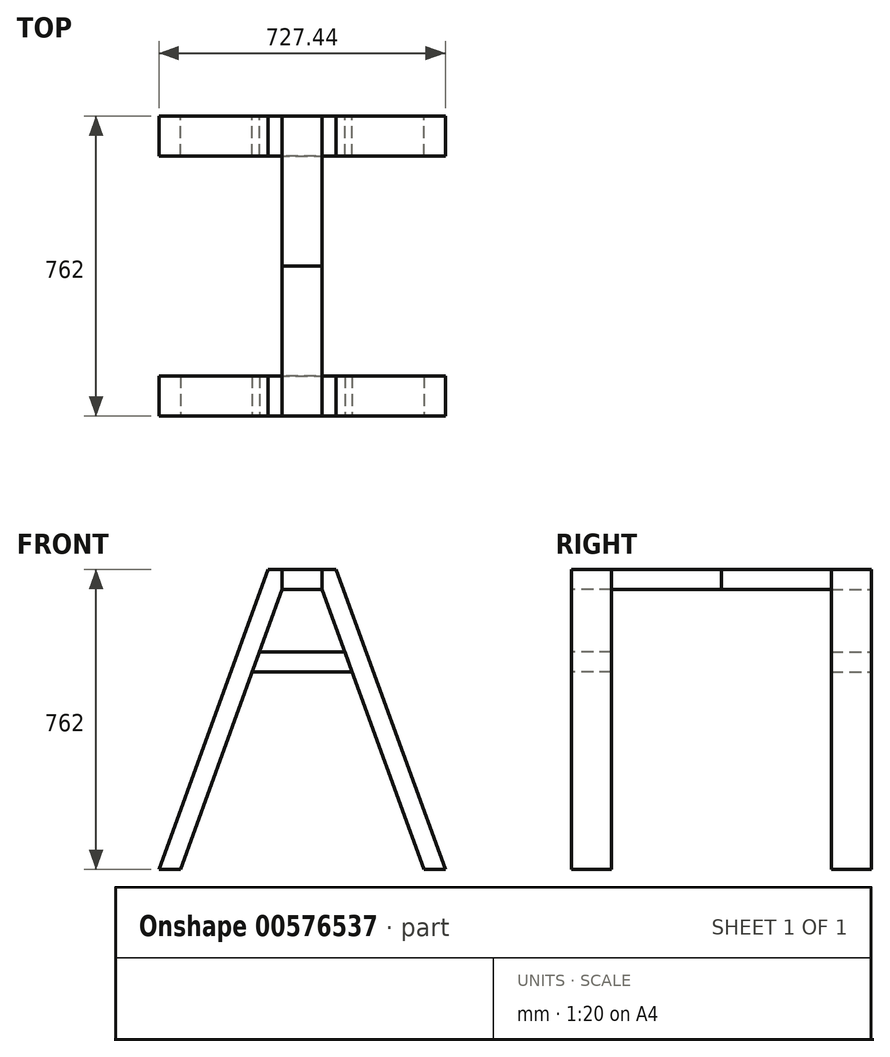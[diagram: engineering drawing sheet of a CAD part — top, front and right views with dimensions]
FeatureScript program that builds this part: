
annotation { "Feature Type Name" : "Feature", "Feature Type Description" : "" }
export const myFeature = defineFeature(function(context is Context, id is Id, definition is map)
    precondition{}
    {
        {
            var Q0;
            Q0=qCreatedBy(makeId("Front.planeOp"),FACE);
            var sketch = newSketch(context, id + "F0", { "sketchPlane" : qUnion([Q0])});
            skLineSegment(sketch, "E0.bottom", {"start": v(0, 0) * mm, "end": v(50.8, 0) * mm});
            skLineSegment(sketch, "E0.top", {"start": v(-35.57, 50.8) * mm, "end": v(50.8, 50.8) * mm});
            skLineSegment(sketch, "E0.left", {"start": v(0, 0) * mm, "end": v(0, 50.8) * mm});
            skLineSegment(sketch, "E1", {"start": v(-35.57, 50.8) * mm, "end": v(-312.92, -711.2) * mm});
            skLineSegment(sketch, "E2", {"start": v(0, 0) * mm, "end": v(-258.86, -711.2) * mm});
            skLineSegment(sketch, "E3", {"start": v(-258.86, -711.2) * mm, "end": v(-312.92, -711.2) * mm});
            skLineSegment(sketch, "E4", {"start": v(50.8, -590.08) * mm, "end": v(50.8, 118.93) * mm, "construction": true});
            skPoint(sketch, "E4.startSnap0", {"position": v(50.8, 0) * mm});
            skPoint(sketch, "E0.right.start.orphan", {"position": v(101.6, 0) * mm});
            skLineSegment(sketch, "E5", {"start": v(50.8, 50.8) * mm, "end": v(50.8, 0) * mm});
            skLineSegment(sketch, "E6.MirrorCS", {"start": v(101.6, 0) * mm, "end": v(101.6, 50.8) * mm});
            skLineSegment(sketch, "E7.MirrorCS", {"start": v(101.6, 0) * mm, "end": v(50.8, 0) * mm});
            skLineSegment(sketch, "E8.MirrorCS", {"start": v(137.17, 50.8) * mm, "end": v(414.52, -711.2) * mm});
            skLineSegment(sketch, "E9.MirrorCS", {"start": v(360.46, -711.2) * mm, "end": v(414.52, -711.2) * mm});
            skLineSegment(sketch, "E10.MirrorCS", {"start": v(101.6, 0) * mm, "end": v(360.46, -711.2) * mm});
            skLineSegment(sketch, "E11.MirrorCS", {"start": v(137.17, 50.8) * mm, "end": v(50.8, 50.8) * mm});
            skLineSegment(sketch, "E12", {"start": v(-57.71, -158.56) * mm, "end": v(159.31, -158.56) * mm});
            skLineSegment(sketch, "E13", {"start": v(177.8, -209.36) * mm, "end": v(-76.2, -209.36) * mm});
            skLineSegment(sketch, "E14", {"start": v(101.6, 0) * mm, "end": v(83.11, 50.8) * mm, "construction": true});
            skLineSegment(sketch, "E15", {"start": v(83.11, 50.8) * mm, "end": v(130.85, 68.17) * mm, "construction": true});
            skLineSegment(sketch, "E16", {"start": v(130.85, 68.17) * mm, "end": v(137.17, 50.8) * mm, "construction": true});
            skLineSegment(sketch, "E17", {"start": v(360.46, -711.2) * mm, "end": v(366.78, -728.57) * mm, "construction": true});
            skLineSegment(sketch, "E18", {"start": v(366.78, -728.57) * mm, "end": v(414.52, -711.2) * mm, "construction": true});
            skLineSegment(sketch, "E19", {"start": v(159.31, -158.56) * mm, "end": v(177.8, -158.56) * mm, "construction": true});
            skLineSegment(sketch, "E20", {"start": v(177.8, -158.56) * mm, "end": v(177.8, -209.36) * mm, "construction": true});
            skLineSegment(sketch, "E21", {"start": v(-57.71, -158.56) * mm, "end": v(-76.2, -158.56) * mm, "construction": true});
            skLineSegment(sketch, "E22", {"start": v(-76.2, -158.56) * mm, "end": v(-76.2, -209.36) * mm, "construction": true});
            skSolve(sketch);
        }
        {
            var Q0;
            Q0=makeQuery(id+"F0.imprint","IMPRINT",FACE,{"disambiguationData":[TD([[makeQuery(id+"F0.imprint","IMPRINT",EDGE,{"derivedFrom":sQuery(id+"F0.wireOp",EDGE,"E0.bottom")}),1.0]])]});
            var Q1;
            {var subQ0=sQuery(id+"F0.wireOp",EDGE,"E5");Q1=makeQuery(id+"F0.imprint","IMPRINT",FACE,{"disambiguationData":[TD([[makeQuery(id+"F0.imprint","IMPRINT",EDGE,{"derivedFrom":subQ0}),1.0]])]});}
            extrude(context, id + "F1", {"entities" : qUnion([Q0, Q1]), "oppositeDirection" : true, "depth" : 381 * mm, "offsetDistance" : 25.4 * mm});
        }
        {
            var Q0;
            {var subQ1=sQuery(id+"F0.wireOp",EDGE,"E6.MirrorCS");Q0=makeQuery(id+"F0.imprint","IMPRINT",FACE,{"disambiguationData":[TD([[makeQuery(id+"F0.imprint","IMPRINT",EDGE,{"derivedFrom":subQ1}),-1.0]])]});}
            var Q1;
            {var subQ1=sQuery(id+"F0.wireOp",EDGE,"E0.left");Q1=makeQuery(id+"F0.imprint","IMPRINT",FACE,{"disambiguationData":[TD([[makeQuery(id+"F0.imprint","IMPRINT",EDGE,{"derivedFrom":subQ1}),1.0]])]});}
            extrude(context, id + "F2", {"entities" : qUnion([Q0, Q1]), "oppositeDirection" : true, "depth" : 101.6 * mm, "offsetDistance" : 25.4 * mm});
        }
        {
            var Q0;
            {var subQ0=sQuery(id+"F0.wireOp",EDGE,"E12");Q0=makeQuery(id+"F0.imprint","IMPRINT",FACE,{"disambiguationData":[TD([[makeQuery(id+"F0.imprint","IMPRINT",EDGE,{"derivedFrom":subQ0}),-1.0]])]});}
            extrude(context, id + "F3", {"entities" : qUnion([Q0]), "oppositeDirection" : true, "depth" : 101.6 * mm, "offsetDistance" : 25.4 * mm});
        }
        {
            var Q0;
            Q0=makeQuery(id+"F1.opExtrude","CAP_FACE",FACE,{"disambiguationData":[OSD([sQuery(id+"F0.wireOp",EDGE,"E0.bottom"),sQuery(id+"F0.wireOp",EDGE,"E0.top"),sQuery(id+"F0.wireOp",EDGE,"E0.left"),sQuery(id+"F0.wireOp",EDGE,"E6.MirrorCS"),sQuery(id+"F0.wireOp",EDGE,"E7.MirrorCS"),sQuery(id+"F0.wireOp",EDGE,"E11.MirrorCS")])],"isStart":false});
            cPlane(context, id + "F4", {"entities" : qUnion([Q0]), "cplaneType" : CPlaneType.OFFSET, "offset" : 0 * mm, "width" : 152.4 * mm, "height" : 152.4 * mm});
        }
        {
            var Q0;
            Q0=makeQuery(id+"F1.opExtrude","SWEPT_BODY",BODY,{"disambiguationData":[OSD([sQuery(id+"F0.wireOp",EDGE,"E0.bottom"),sQuery(id+"F0.wireOp",EDGE,"E0.top"),sQuery(id+"F0.wireOp",EDGE,"E0.left"),sQuery(id+"F0.wireOp",EDGE,"E6.MirrorCS"),sQuery(id+"F0.wireOp",EDGE,"E7.MirrorCS"),sQuery(id+"F0.wireOp",EDGE,"E11.MirrorCS")])]});
            var Q1;
            Q1=makeQuery(id+"F2.opExtrude","SWEPT_BODY",BODY,{"disambiguationData":[OSD([sQuery(id+"F0.wireOp",EDGE,"E0.top"),sQuery(id+"F0.wireOp",EDGE,"E0.left"),sQuery(id+"F0.wireOp",EDGE,"E1"),sQuery(id+"F0.wireOp",EDGE,"E2"),sQuery(id+"F0.wireOp",EDGE,"E3")])]});
            var Q2;
            Q2=makeQuery(id+"F2.opExtrude","SWEPT_BODY",BODY,{"disambiguationData":[OSD([sQuery(id+"F0.wireOp",EDGE,"E6.MirrorCS"),sQuery(id+"F0.wireOp",EDGE,"E8.MirrorCS"),sQuery(id+"F0.wireOp",EDGE,"E9.MirrorCS"),sQuery(id+"F0.wireOp",EDGE,"E10.MirrorCS"),sQuery(id+"F0.wireOp",EDGE,"E11.MirrorCS")])]});
            var Q3;
            Q3=makeQuery(id+"F3.opExtrude","SWEPT_BODY",BODY,{"disambiguationData":[OSD([sQuery(id+"F0.wireOp",EDGE,"E2"),sQuery(id+"F0.wireOp",EDGE,"E10.MirrorCS"),sQuery(id+"F0.wireOp",EDGE,"E12"),sQuery(id+"F0.wireOp",EDGE,"E13")])]});
            var Q4;
            Q4=qCreatedBy(id+"F4.planeOp",FACE);
            mirror(context, id + "F5", {"entities" : qUnion([Q0, Q1, Q2, Q3]), "mirrorPlane" : qUnion([Q4])});
        }
    });
